# Revit family: Haworth_HATElements_Screen_Frameless_AP_PRELIMINARY
name_source: partatom
category: Furniture
units: mm (PartAtom-declared; Revit-internal decimal feet)

## family parameters
Always vertical = Yes
Cut with Voids When Loaded = No
Room Calculation Point = No
Shared = No
Work Plane-Based = No

## types (1)
- Screen - Frameless
    Actual Depth = 20 mm  [stored 0.0656168 ft]
    Actual Height = 600 mm
    Actual Width = 1800 mm  [stored 5.90551 ft]
    Description = Haworth - HAT Elements - Screen Frameless
    Fixing Kit Finish = Haworth _ Polymer _ Undecided
    Hanged Kit = Yes
    Manufacturer = Haworth, Inc.
    Model = SYELXXXXXX
    Revision Number = 1
    Size = Verify Final Dim. w/Haworth
    Standard Widths = 1200, 1400, 1500, 1600, 1800 mm
    Standing Kit = No
    URL = https://www.haworth.com
    URL - Product = https://www.haworth.com
    Warranty = http://www.haworth.com

note: [stored X ft] marks values corroborated as IEEE doubles in the binary element streams (Revit-internal decimal feet)

## geometry (parser evidence)
native form markers: Sweep x6
no freeform markers — native parametric forms only
